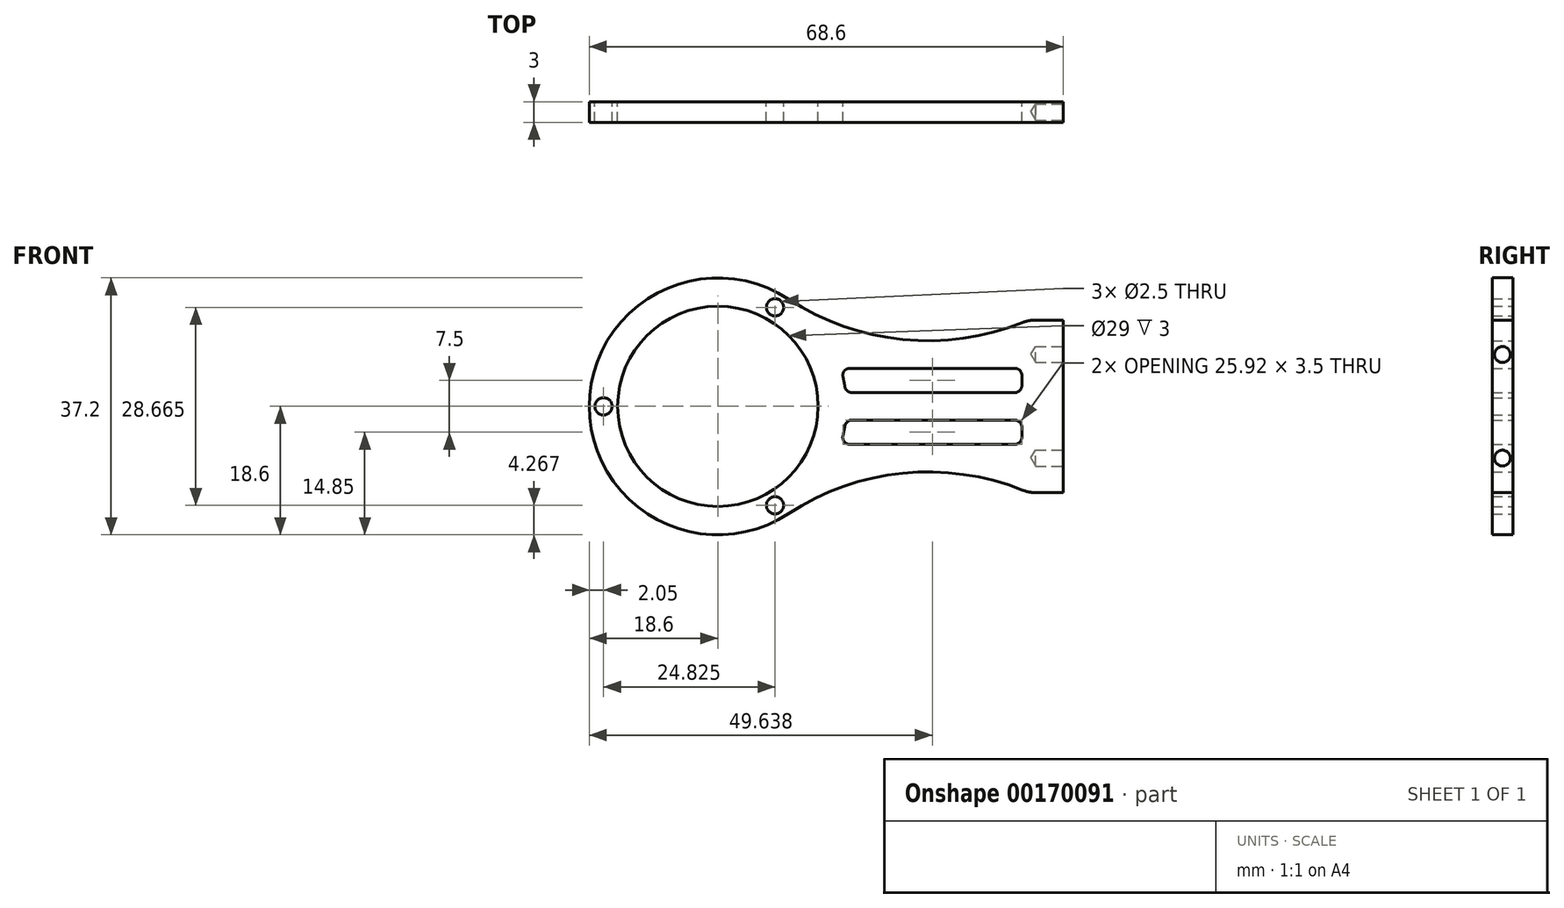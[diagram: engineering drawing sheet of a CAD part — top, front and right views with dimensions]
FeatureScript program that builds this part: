
annotation { "Feature Type Name" : "Feature", "Feature Type Description" : "" }
export const myFeature = defineFeature(function(context is Context, id is Id, definition is map)
    precondition{}
    {
        {
            var Q0;
            Q0=qCreatedBy(makeId("Front.planeOp"),FACE);
            var sketch = newSketch(context, id + "F0", { "sketchPlane" : qUnion([Q0])});
            skCircle(sketch, "E0", {"center": v(0, 0) * mm, "radius": 16.55 * mm, "construction": true});
            skCircle(sketch, "E1", {"center": v(0, 0) * mm, "radius": 14.5 * mm});
            skCircle(sketch, "E2", {"center": v(0, 0) * mm, "radius": 18.6 * mm});
            skLineSegment(sketch, "E3", {"start": v(0, 0) * mm, "end": v(50, 0) * mm, "construction": true});
            skLineSegment(sketch, "E4", {"start": v(50, 12.5) * mm, "end": v(50, -12.5) * mm});
            skLineSegment(sketch, "E5", {"start": v(50, 12.5) * mm, "end": v(45, 12.5) * mm});
            skLineSegment(sketch, "E6", {"start": v(45, 12.5) * mm, "end": v(45, -12.5) * mm, "construction": true});
            skLineSegment(sketch, "E7", {"start": v(45, -12.5) * mm, "end": v(50, -12.5) * mm});
            skLineSegment(sketch, "E8", {"start": v(-16.55, 0) * mm, "end": v(0, 0) * mm, "construction": true});
            skLineSegment(sketch, "E9", {"start": v(8.27, 14.33) * mm, "end": v(0, 0) * mm, "construction": true});
            skLineSegment(sketch, "E10", {"start": v(8.27, -14.33) * mm, "end": v(0, 0) * mm, "construction": true});
            skLineSegment(sketch, "E11", {"start": v(0, 14.5) * mm, "end": v(0, 16.55) * mm, "construction": true});
            skLineSegment(sketch, "E12", {"start": v(0, 16.55) * mm, "end": v(0, 18.6) * mm, "construction": true});
            skArc(sketch, "E13", {"start": v(10.2, 15.55) * mm, "mid": v(27.22, 9.64) * mm, "end": v(45, 12.5) * mm});
            skArc(sketch, "E14.MirrorCS", {"start": v(10.2, -15.55) * mm, "mid": v(27.22, -9.64) * mm, "end": v(45, -12.5) * mm});
            skPoint(sketch, "E15", {"position": v(-16.55, 0) * mm});
            skPoint(sketch, "E16", {"position": v(8.27, -14.33) * mm});
            skPoint(sketch, "E17", {"position": v(8.27, 14.33) * mm});
            skLineSegment(sketch, "E18.bottom", {"start": v(17.77, 5.5) * mm, "end": v(44, 5.5) * mm});
            skLineSegment(sketch, "E18.top", {"start": v(18.5, 2) * mm, "end": v(44, 2) * mm});
            skLineSegment(sketch, "E18.right", {"start": v(44, 5.5) * mm, "end": v(44, 2) * mm});
            skLineSegment(sketch, "E19.MirrorCS", {"start": v(44, -5.5) * mm, "end": v(44, -2) * mm});
            skLineSegment(sketch, "E20.MirrorCS", {"start": v(18.5, -2) * mm, "end": v(44, -2) * mm});
            skLineSegment(sketch, "E21.MirrorCS", {"start": v(17.77, -5.5) * mm, "end": v(44, -5.5) * mm});
            skLineSegment(sketch, "E22", {"start": v(30.44, 9.5) * mm, "end": v(30.44, 5.5) * mm, "construction": true});
            skLineSegment(sketch, "E23", {"start": v(30.44, 2) * mm, "end": v(30.44, -2) * mm, "construction": true});
            skLineSegment(sketch, "E24", {"start": v(30.44, -5.5) * mm, "end": v(30.44, -9.5) * mm, "construction": true});
            skSolve(sketch);
        }
        {
            var Q0;
            Q0=makeQuery(id+"F0.imprint","IMPRINT",FACE,{"disambiguationData":[TD([[makeQuery(id+"F0.imprint","IMPRINT",EDGE,{"derivedFrom":sQuery(id+"F0.wireOp",EDGE,"E1")}),-1.0]])]});
            var Q1;
            Q1=makeQuery(id+"F0.imprint","IMPRINT",FACE,{"disambiguationData":[TD([[makeQuery(id+"F0.imprint","IMPRINT",EDGE,{"derivedFrom":sQuery(id+"F0.wireOp",EDGE,"E4")}),-1.0]])]});
            extrude(context, id + "F1", {"entities" : qUnion([Q0, Q1]), "depth" : 3 * mm});
        }
        {
            var Q0;
            Q0=sQuery(id+"F0.wireOp",VERTEX,"E15");
            var Q1;
            Q1=sQuery(id+"F0.wireOp",VERTEX,"E16");
            var Q2;
            Q2=sQuery(id+"F0.wireOp",VERTEX,"E17");
            var Q3;
            Q3=makeQuery(id+"F1.opExtrude","SWEPT_BODY",BODY,{"disambiguationData":[OSD([sQuery(id+"F0.wireOp",EDGE,"E1"),sQuery(id+"F0.wireOp",EDGE,"E2"),sQuery(id+"F0.wireOp",EDGE,"E4"),sQuery(id+"F0.wireOp",EDGE,"E5"),sQuery(id+"F0.wireOp",EDGE,"E7"),sQuery(id+"F0.wireOp",EDGE,"E13"),sQuery(id+"F0.wireOp",EDGE,"E14.MirrorCS")])]});
            hole(context, id + "F2", {"style" : HoleStyle.SIMPLE, "endStyle" : HoleEndStyle.THROUGH, "oppositeDirection" : true, "holeDiameter" : 2.5 * mm, "locations" : qUnion([Q0, Q1, Q2]), "scope" : qUnion([Q3]), "isTappedThrough" : true});
        }
        {
            var Q0;
            Q0=makeQuery(id+"F1.opExtrude","SWEPT_EDGE",EDGE,{"disambiguationData":[OSD([sQuery(id+"F0.wireOp",EDGE,"E2"),sQuery(id+"F0.wireOp",EDGE,"E18.bottom")])]});
            var Q1;
            Q1=makeQuery(id+"F1.opExtrude","SWEPT_EDGE",EDGE,{"disambiguationData":[OSD([sQuery(id+"F0.wireOp",EDGE,"E2"),sQuery(id+"F0.wireOp",EDGE,"E20.MirrorCS")])]});
            var Q2;
            Q2=makeQuery(id+"F1.opExtrude","SWEPT_EDGE",EDGE,{"disambiguationData":[OSD([sQuery(id+"F0.wireOp",EDGE,"E2"),sQuery(id+"F0.wireOp",EDGE,"E18.top")])]});
            var Q3;
            Q3=makeQuery(id+"F1.opExtrude","SWEPT_EDGE",EDGE,{"disambiguationData":[OSD([sQuery(id+"F0.wireOp",EDGE,"E2"),sQuery(id+"F0.wireOp",EDGE,"E21.MirrorCS")])]});
            var Q4;
            Q4=makeQuery(id+"F1.opExtrude","SWEPT_EDGE",EDGE,{"disambiguationData":[OSD([sQuery(id+"F0.wireOp",EDGE,"E19.MirrorCS"),sQuery(id+"F0.wireOp",EDGE,"E20.MirrorCS")])]});
            var Q5;
            Q5=makeQuery(id+"F1.opExtrude","SWEPT_EDGE",EDGE,{"disambiguationData":[OSD([sQuery(id+"F0.wireOp",EDGE,"E18.bottom"),sQuery(id+"F0.wireOp",EDGE,"E18.right")])]});
            var Q6;
            Q6=makeQuery(id+"F1.opExtrude","SWEPT_EDGE",EDGE,{"disambiguationData":[OSD([sQuery(id+"F0.wireOp",EDGE,"E18.top"),sQuery(id+"F0.wireOp",EDGE,"E18.right")])]});
            var Q7;
            Q7=makeQuery(id+"F1.opExtrude","SWEPT_EDGE",EDGE,{"disambiguationData":[OSD([sQuery(id+"F0.wireOp",EDGE,"E19.MirrorCS"),sQuery(id+"F0.wireOp",EDGE,"E21.MirrorCS")])]});
            fillet(context, id + "F3", {"entities" : qUnion([Q0, Q1, Q2, Q3, Q4, Q5, Q6, Q7]), "radius" : 1 * mm, "tangentPropagation" : true, "allowEdgeOverflow" : false});
        }
        {
            var Q0;
            Q0=makeQuery(id+"F1.opExtrude","SWEPT_EDGE",EDGE,{"disambiguationData":[OSD([sQuery(id+"F0.wireOp",EDGE,"E5"),sQuery(id+"F0.wireOp",EDGE,"E13")])]});
            var Q1;
            Q1=makeQuery(id+"F1.opExtrude","SWEPT_EDGE",EDGE,{"disambiguationData":[OSD([sQuery(id+"F0.wireOp",EDGE,"E7"),sQuery(id+"F0.wireOp",EDGE,"E14.MirrorCS")])]});
            fillet(context, id + "F4", {"entities" : qUnion([Q0, Q1]), "radius" : 5 * mm, "tangentPropagation" : true, "allowEdgeOverflow" : false});
        }
        {
            var Q0;
            Q0=makeQuery(id+"F1.opExtrude","SWEPT_FACE",FACE,{"disambiguationData":[OSD([sQuery(id+"F0.wireOp",EDGE,"E4")])]});
            var sketch = newSketch(context, id + "F5", { "sketchPlane" : qUnion([Q0])});
            skLineSegment(sketch, "E25", {"start": v(-1.5, 7.5) * mm, "end": v(-1.5, -7.5) * mm, "construction": true});
            skLineSegment(sketch, "E26", {"start": v(-1.5, 0) * mm, "end": v(0, 0) * mm, "construction": true});
            skLineSegment(sketch, "E27", {"start": v(-1.5, 0) * mm, "end": v(-3, 0) * mm, "construction": true});
            skPoint(sketch, "E28", {"position": v(-1.5, 7.5) * mm});
            skPoint(sketch, "E29", {"position": v(-1.5, -7.5) * mm});
            skSolve(sketch);
        }
        {
            var Q0;
            Q0=sQuery(id+"F5.wireOp",VERTEX,"E28");
            var Q1;
            Q1=sQuery(id+"F5.wireOp",VERTEX,"E29");
            var Q2;
            Q2=makeQuery(id+"F1.opExtrude","SWEPT_BODY",BODY,{"disambiguationData":[OSD([sQuery(id+"F0.wireOp",EDGE,"E1"),sQuery(id+"F0.wireOp",EDGE,"E2"),sQuery(id+"F0.wireOp",EDGE,"E4"),sQuery(id+"F0.wireOp",EDGE,"E5"),sQuery(id+"F0.wireOp",EDGE,"E7"),sQuery(id+"F0.wireOp",EDGE,"E13"),sQuery(id+"F0.wireOp",EDGE,"E14.MirrorCS"),sQuery(id+"F0.wireOp",EDGE,"E18.bottom"),sQuery(id+"F0.wireOp",EDGE,"E18.top"),sQuery(id+"F0.wireOp",EDGE,"E18.right"),sQuery(id+"F0.wireOp",EDGE,"E19.MirrorCS"),sQuery(id+"F0.wireOp",EDGE,"E20.MirrorCS"),sQuery(id+"F0.wireOp",EDGE,"E21.MirrorCS")])]});
            hole(context, id + "F6", {"style" : HoleStyle.SIMPLE, "endStyle" : HoleEndStyle.BLIND, "holeDiameter" : 2.3 * mm, "holeDepth" : 4 * mm, "locations" : qUnion([Q0, Q1]), "scope" : qUnion([Q2])});
        }
    });
